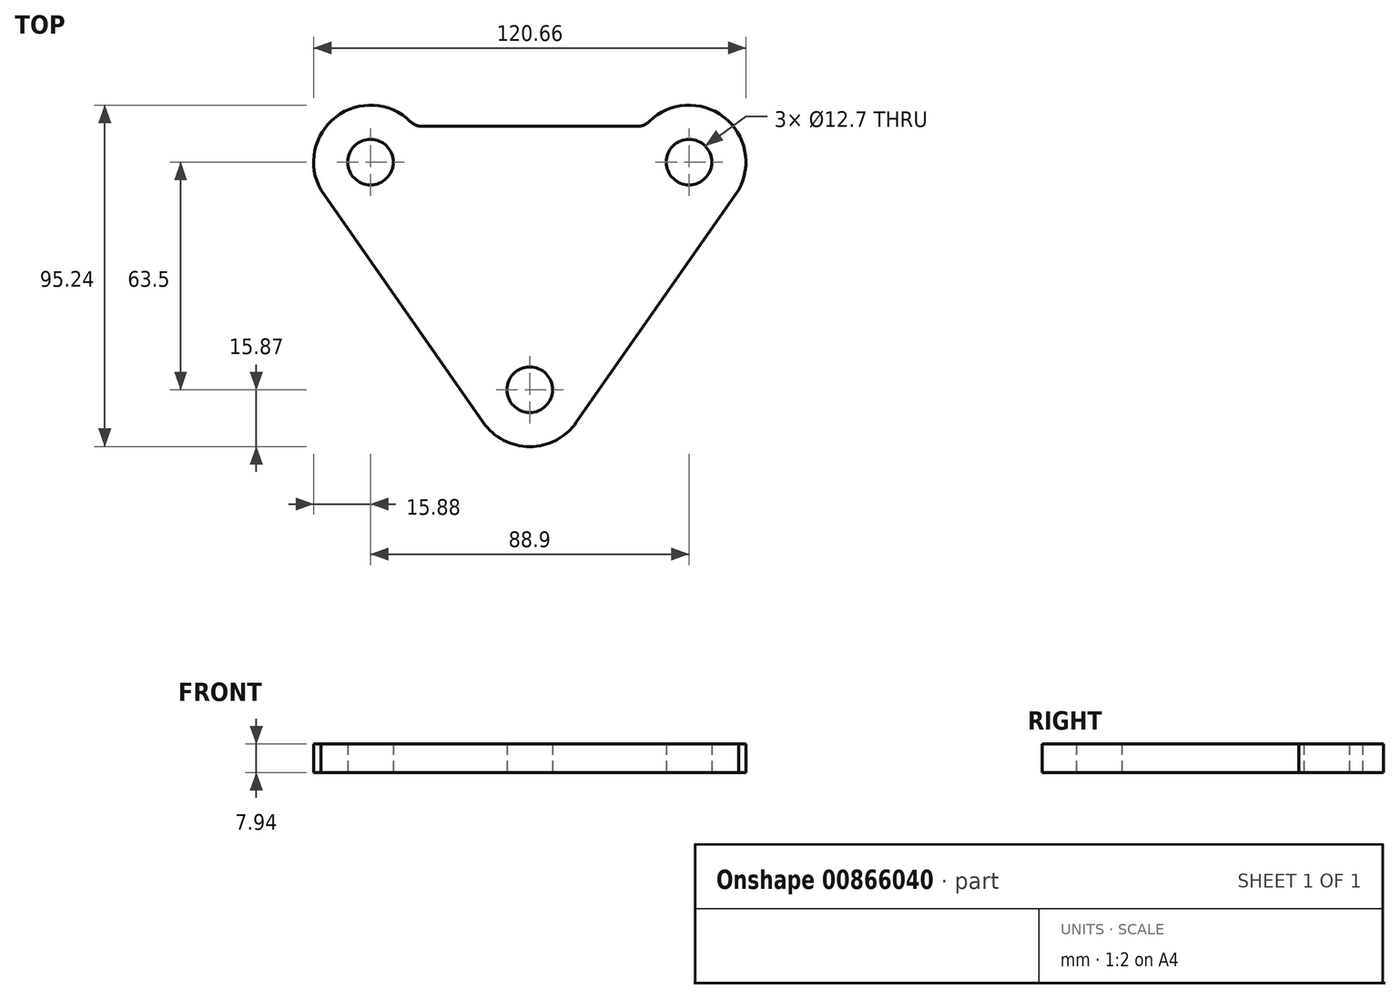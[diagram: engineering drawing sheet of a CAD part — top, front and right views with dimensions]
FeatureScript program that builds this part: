
annotation { "Feature Type Name" : "Feature", "Feature Type Description" : "" }
export const myFeature = defineFeature(function(context is Context, id is Id, definition is map)
    precondition{}
    {
        {
            var Q0;
            Q0=qCreatedBy(makeId("Top.planeOp"),FACE);
            var sketch = newSketch(context, id + "F0", { "sketchPlane" : qUnion([Q0])});
            skArc(sketch, "E0", {"start": v(-13.01, -9.1) * mm, "mid": v(0, -15.88) * mm, "end": v(13.01, -9.1) * mm});
            skArc(sketch, "E1", {"start": v(56.53, 53.2) * mm, "mid": v(55.28, 75.1) * mm, "end": v(33.34, 74.84) * mm});
            skArc(sketch, "E2", {"start": v(-33.34, 74.84) * mm, "mid": v(-55.28, 75.1) * mm, "end": v(-56.53, 53.2) * mm});
            skCircle(sketch, "E3", {"center": v(-44.45, 63.5) * mm, "radius": 6.35 * mm});
            skCircle(sketch, "E4", {"center": v(44.45, 63.5) * mm, "radius": 6.35 * mm});
            skCircle(sketch, "E5", {"center": v(0, 0) * mm, "radius": 6.35 * mm});
            skLineSegment(sketch, "E6", {"start": v(30, 73.48) * mm, "end": v(-30, 73.48) * mm});
            skPoint(sketch, "E7.orphan", {"position": v(0, 63.5) * mm});
            skLineSegment(sketch, "E8", {"start": v(-58.28, 55.7) * mm, "end": v(-13.01, -9.1) * mm});
            skLineSegment(sketch, "E9", {"start": v(58.28, 55.7) * mm, "end": v(13.01, -9.1) * mm});
            skPoint(sketch, "E10.visualSharp", {"position": v(-32.1, 73.48) * mm});
            skArc(sketch, "E10.filletArc", {"start": v(-33.34, 74.84) * mm, "mid": v(-31.8, 73.83) * mm, "end": v(-30, 73.48) * mm});
            skPoint(sketch, "E11.visualSharp", {"position": v(32.1, 73.48) * mm});
            skArc(sketch, "E11.filletArc", {"start": v(30, 73.48) * mm, "mid": v(31.8, 73.83) * mm, "end": v(33.34, 74.84) * mm});
            skSolve(sketch);
        }
        {
            var Q0;
            {var subQ1=sQuery(id+"F0.wireOp",EDGE,"E0");Q0=makeQuery(id+"F0.imprint","IMPRINT",FACE,{"disambiguationData":[TD([[makeQuery(id+"F0.imprint","IMPRINT",EDGE,{"derivedFrom":subQ1}),1.0]])]});}
            extrude(context, id + "F1", {"entities" : qUnion([Q0]), "depth" : 7.94 * mm, "offsetDistance" : 25.4 * mm});
        }
    });
